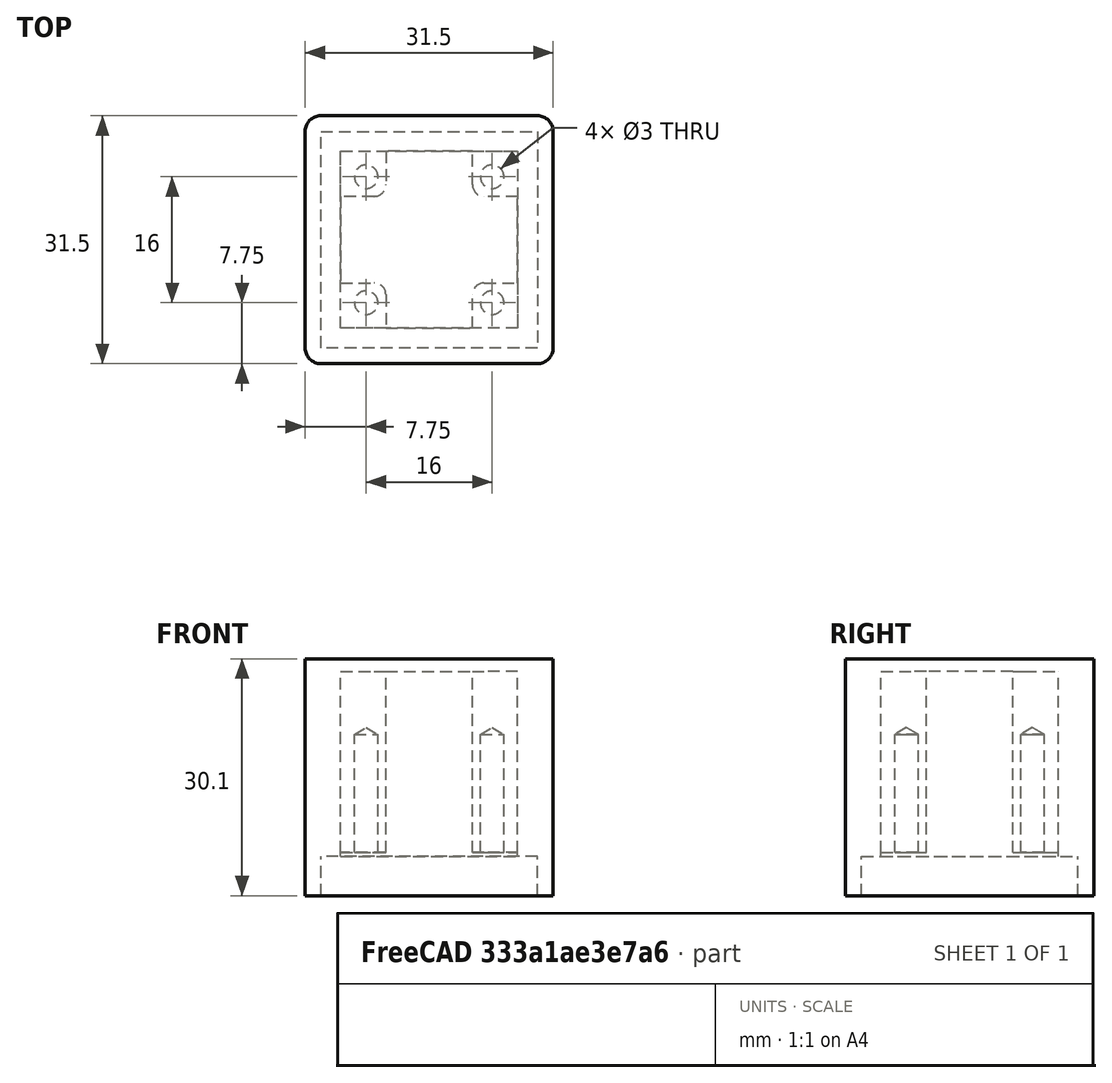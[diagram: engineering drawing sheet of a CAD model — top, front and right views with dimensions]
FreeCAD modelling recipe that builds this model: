
FCSTD DOCUMENT  (FreeCAD 1.1R44874 (Git))
Label: hood1slim_10x10x20
objects: Sketcher::SketchObject×6, PartDesign::Pocket×3, App::Point×1, PartDesign::Pad×1, PartDesign::Hole×1, Mesh::Feature×1, PartDesign::Body×1
note: 28 computed .brp shape members not serialized (recipe doc carries the construction recipe); baked Part::Feature solids carry a one-line shape summary decoded from their .brp

FEATURE [App::Point] Origin001
  Role = Origin
FEATURE [Sketcher::SketchObject] Sketch
  ArcFitTolerance = 1e-06
  AttachmentSupport = -> [Origin]
  ExternalTypes = [0]
  FullyConstrained = true
  MakeInternals = false
  MapMode = 5
  _ExternalGeoVersion = 1
  sketch-geometry (13):
    g0: LineSegment StartX=-13.75 StartY=-15.75 StartZ=0 EndX=13.75 EndY=-15.75 EndZ=0
    g1: LineSegment StartX=15.75 StartY=-13.75 StartZ=0 EndX=15.75 EndY=13.75 EndZ=0
    g2: LineSegment StartX=13.75 StartY=15.75 StartZ=0 EndX=-13.75 EndY=15.75 EndZ=0
    g3: LineSegment StartX=-15.75 StartY=13.75 StartZ=0 EndX=-15.75 EndY=-13.75 EndZ=0
    g4: GeomPoint [constr] X=0 Y=0 Z=0
    g5: ArcOfCircle CenterX=-13.75 CenterY=13.75 CenterZ=0 NormalX=0 NormalY=0 NormalZ=1 AngleXU=0 Radius=2 StartAngle=1.5708 EndAngle=3.14159
    g6: GeomPoint [constr] X=-15.75 Y=15.75 Z=0
    g7: ArcOfCircle CenterX=13.75 CenterY=13.75 CenterZ=0 NormalX=0 NormalY=0 NormalZ=1 AngleXU=0 Radius=2 StartAngle=0 EndAngle=1.5708
    g8: GeomPoint [constr] X=15.75 Y=15.75 Z=0
    g9: ArcOfCircle CenterX=13.75 CenterY=-13.75 CenterZ=0 NormalX=0 NormalY=0 NormalZ=1 AngleXU=0 Radius=2 StartAngle=4.71239 EndAngle=6.28319
    g10: GeomPoint [constr] X=15.75 Y=-15.75 Z=0
    g11: ArcOfCircle CenterX=-13.75 CenterY=-13.75 CenterZ=0 NormalX=0 NormalY=0 NormalZ=1 AngleXU=0 Radius=2 StartAngle=3.14159 EndAngle=4.71239
    g12: GeomPoint [constr] X=-15.75 Y=-15.75 Z=0
  constraints (28):
    c: Horizontal(g0)
    c: Horizontal(g2)
    c: Vertical(g1)
    c: Vertical(g3)
    c: Symmetric(g8,g12,g4)
    c: Distance(g10,g12) = 31.5
    c: Distance(g12,g6) = 31.5
    c: Coincident(g4,g-1)
    c: PointOnObject(g6,g3)
    c: PointOnObject(g6,g2)
    c: Tangent(g3,g5) = -1.5708
    c: Tangent(g2,g5) = -1.5708
    c: Radius(g5) = 2
    c: PointOnObject(g8,g1)
    c: PointOnObject(g8,g2)
    c: Tangent(g1,g7) = -1.5708
    c: Tangent(g2,g7) = -1.5708
    c: PointOnObject(g10,g1)
    c: PointOnObject(g10,g0)
    c: Tangent(g1,g9) = -1.5708
    c: Tangent(g0,g9) = -1.5708
    c: PointOnObject(g12,g0)
    c: PointOnObject(g12,g3)
    c: Tangent(g0,g11) = -1.5708
    c: Tangent(g3,g11) = -1.5708
    c: Equal(g5,g7)
    c: Equal(g5,g11)
    c: Equal(g5,g9)
FEATURE [PartDesign::Pad] Pad
  Direction = (0,0,1)
  Length = 30.1
  Length2 = 10
  Profile = -> Sketch
  ReferenceAxis = -> Sketch [N_Axis]
  Refine = true
  SideType = 0
  Suppressed = false
  Type = 0
  Type2 = 0
FEATURE [Sketcher::SketchObject] Sketch001
  ArcFitTolerance = 1e-06
  AttachmentSupport = -> [Pad]
  ExternalTypes = [0]
  FullyConstrained = true
  MakeInternals = false
  MapMode = 5
  Placement = pos=(0,0,0) rot=(1,0,0;3.14159rad)
  _ExternalGeoVersion = 1
  sketch-geometry (5):
    g0: LineSegment StartX=-13.75 StartY=-13.75 StartZ=0 EndX=13.75 EndY=-13.75 EndZ=0
    g1: LineSegment StartX=13.75 StartY=-13.75 StartZ=0 EndX=13.75 EndY=13.75 EndZ=0
    g2: LineSegment StartX=13.75 StartY=13.75 StartZ=0 EndX=-13.75 EndY=13.75 EndZ=0
    g3: LineSegment StartX=-13.75 StartY=13.75 StartZ=0 EndX=-13.75 EndY=-13.75 EndZ=0
    g4: GeomPoint [constr] X=0 Y=0 Z=0
  constraints (12):
    c: Coincident(g0,g1)
    c: Coincident(g1,g2)
    c: Coincident(g2,g3)
    c: Coincident(g3,g0)
    c: Horizontal(g0)
    c: Horizontal(g2)
    c: Vertical(g1)
    c: Vertical(g3)
    c: Symmetric(g2,g0,g4)
    c: Distance(g1,g3) = 27.5
    c: Distance(g0,g2) = 27.5
    c: Coincident(g4,g-1)
FEATURE [PartDesign::Pocket] Pocket
  BaseFeature = -> Pad
  Direction = (0,0,1)
  Length = 5
  Length2 = 5
  Profile = -> Sketch001
  ReferenceAxis = -> Sketch001 [N_Axis]
  Refine = true
  SideType = 0
  Suppressed = false
  Type = 0
  Type2 = 0
FEATURE [Sketcher::SketchObject] Sketch002
  ArcFitTolerance = 1e-06
  AttachmentSupport = -> [Pocket]
  ExternalTypes = [0]
  FullyConstrained = true
  MakeInternals = false
  MapMode = 5
  Placement = pos=(0,0,5) rot=(1,0,0;3.14159rad)
  _ExternalGeoVersion = 1
  sketch-geometry (5):
    g0: LineSegment StartX=-11.25 StartY=-11.25 StartZ=0 EndX=11.25 EndY=-11.25 EndZ=0
    g1: LineSegment StartX=11.25 StartY=-11.25 StartZ=0 EndX=11.25 EndY=11.25 EndZ=0
    g2: LineSegment StartX=11.25 StartY=11.25 StartZ=0 EndX=-11.25 EndY=11.25 EndZ=0
    g3: LineSegment StartX=-11.25 StartY=11.25 StartZ=0 EndX=-11.25 EndY=-11.25 EndZ=0
    g4: GeomPoint [constr] X=0 Y=0 Z=0
  constraints (12):
    c: Coincident(g0,g1)
    c: Coincident(g1,g2)
    c: Coincident(g2,g3)
    c: Coincident(g3,g0)
    c: Horizontal(g0)
    c: Horizontal(g2)
    c: Vertical(g1)
    c: Vertical(g3)
    c: Symmetric(g2,g0,g4)
    c: Distance(g1,g3) = 22.5
    c: Distance(g0,g2) = 22.5
    c: Coincident(g4,g-1)
FEATURE [PartDesign::Pocket] Pocket001
  BaseFeature = -> Pocket
  Direction = (0,0,1)
  Length = 0.5
  Length2 = 5
  Profile = -> Sketch002
  ReferenceAxis = -> Sketch002 [N_Axis]
  Refine = true
  SideType = 0
  Suppressed = false
  Type = 0
  Type2 = 0
FEATURE [Sketcher::SketchObject] Sketch003
  ArcFitTolerance = 1e-06
  AttachmentSupport = -> [Pocket001]
  ExternalTypes = [0]
  FullyConstrained = true
  MakeInternals = false
  MapMode = 5
  Placement = pos=(0,0,5.5) rot=(1,0,0;3.14159rad)
  _ExternalGeoVersion = 1
  sketch-geometry (4):
    g0: Circle CenterX=8 CenterY=8 CenterZ=0 NormalX=0 NormalY=0 NormalZ=1 AngleXU=0 Radius=1.5
    g1: Circle CenterX=-8 CenterY=8 CenterZ=0 NormalX=0 NormalY=0 NormalZ=1 AngleXU=0 Radius=1.5
    g2: Circle CenterX=-8 CenterY=-8 CenterZ=0 NormalX=0 NormalY=0 NormalZ=1 AngleXU=0 Radius=1.5
    g3: Circle CenterX=8 CenterY=-8 CenterZ=0 NormalX=0 NormalY=0 NormalZ=1 AngleXU=0 Radius=1.5
  constraints (9):
    c: Diameter(g0) = 3
    c: DistanceY(g-1,g0) = 8
    c: DistanceX(g-1,g0) = 8
    c: Equal(g0,g1)
    c: Equal(g0,g2)
    c: Equal(g0,g3)
    c: Symmetric(g1,g3,g-1)
    c: Symmetric(g0,g3,g-1)
    c: Symmetric(g2,g3,g-2)
FEATURE [PartDesign::Hole] Hole
  BaseFeature = -> Pocket001
  BaseProfileType = 7
  CustomThreadClearance = 0
  Depth = 15
  DepthType = 0
  Diameter = 3
  DrillForDepth = false
  DrillPoint = 1
  DrillPointAngle = 118
  HoleCutCountersinkAngle = 90
  HoleCutCustomValues = false
  HoleCutDepth = 0
  HoleCutDiameter = 0
  HoleCutType = 0
  ModelThread = false
  Profile = -> Sketch003
  Refine = true
  Suppressed = false
  Tapered = false
  TaperedAngle = 90
  ThreadClass = 0
  ThreadDepth = 15
  ThreadDepthType = 0
  ThreadDiameter = 3
  ThreadDirection = 0
  ThreadFit = 0
  ThreadSize = 0
  ThreadType = 0
  Threaded = false
  UseCustomThreadClearance = false
FEATURE [Sketcher::SketchObject] Sketch004
  ArcFitTolerance = 1e-06
  AttachmentSupport = -> [Hole]
  ExternalGeometry = -> [Sketch002]
  ExternalTypes = [0,0,0,0]
  FullyConstrained = true
  MakeInternals = false
  MapMode = 5
  Placement = pos=(0,0,5.5) rot=(1,0,0;3.14159rad)
  _ExternalGeoVersion = 1
  sketch-geometry (21):
    g0: GeomPoint [constr] X=0 Y=0 Z=0
    g1: LineSegment StartX=-11.25 StartY=-5.5 StartZ=0 EndX=-11.25 EndY=5.5 EndZ=0
    g2: LineSegment StartX=-11.25 StartY=5.5 StartZ=0 EndX=-7 EndY=5.5 EndZ=0
    g3: LineSegment StartX=-5.5 StartY=7 StartZ=0 EndX=-5.5 EndY=11.25 EndZ=0
    g4: LineSegment StartX=-5.5 StartY=11.25 StartZ=0 EndX=5.5 EndY=11.25 EndZ=0
    g5: LineSegment StartX=5.5 StartY=11.25 StartZ=0 EndX=5.5 EndY=7 EndZ=0
    g6: LineSegment StartX=7 StartY=5.5 StartZ=0 EndX=11.25 EndY=5.5 EndZ=0
    g7: LineSegment StartX=11.25 StartY=5.5 StartZ=0 EndX=11.25 EndY=-5.5 EndZ=0
    g8: LineSegment StartX=11.25 StartY=-5.5 StartZ=0 EndX=7 EndY=-5.5 EndZ=0
    g9: LineSegment StartX=5.5 StartY=-7 StartZ=0 EndX=5.5 EndY=-11.25 EndZ=0
    g10: LineSegment StartX=5.5 StartY=-11.25 StartZ=0 EndX=-5.5 EndY=-11.25 EndZ=0
    g11: LineSegment StartX=-5.5 StartY=-11.25 StartZ=0 EndX=-5.5 EndY=-7 EndZ=0
    g12: LineSegment StartX=-7 StartY=-5.5 StartZ=0 EndX=-11.25 EndY=-5.5 EndZ=0
    g13: ArcOfCircle CenterX=-7 CenterY=7 CenterZ=0 NormalX=0 NormalY=0 NormalZ=1 AngleXU=0 Radius=1.5 StartAngle=4.71239 EndAngle=6.28319
    g14: GeomPoint [constr] X=-5.5 Y=5.5 Z=0
    g15: ArcOfCircle CenterX=7 CenterY=7 CenterZ=0 NormalX=0 NormalY=0 NormalZ=1 AngleXU=0 Radius=1.5 StartAngle=3.14159 EndAngle=4.71239
    g16: GeomPoint [constr] X=5.5 Y=5.5 Z=0
    g17: ArcOfCircle CenterX=7 CenterY=-7 CenterZ=0 NormalX=0 NormalY=0 NormalZ=1 AngleXU=0 Radius=1.5 StartAngle=1.5708 EndAngle=3.14159
    g18: GeomPoint [constr] X=5.5 Y=-5.5 Z=0
    g19: ArcOfCircle CenterX=-7 CenterY=-7 CenterZ=0 NormalX=0 NormalY=0 NormalZ=1 AngleXU=0 Radius=1.5 StartAngle=0 EndAngle=1.5708
    g20: GeomPoint [constr] X=-5.5 Y=-5.5 Z=0
  constraints (46):
    c: Coincident(g0,g-1)
    c: Coincident(g1,g2)
    c: Horizontal(g2)
    c: Vertical(g3)
    c: Coincident(g3,g4)
    c: Coincident(g4,g5)
    c: Vertical(g5)
    c: Horizontal(g6)
    c: Coincident(g6,g7)
    c: Coincident(g7,g8)
    c: Vertical(g9)
    c: Coincident(g9,g10)
    c: Coincident(g10,g11)
    c: Coincident(g12,g1)
    c: Tangent(g4,g-3)
    c: Tangent(g1,g-4)
    c: Tangent(g7,g-6)
    c: Tangent(g10,g-5)
    c: DistanceY(g-1,g16) = 5.5
    c: DistanceX(g-1,g16) = 5.5
    c: Symmetric(g16,g18,g-1)
    c: Symmetric(g16,g14,g-2)
    c: Symmetric(g18,g20,g-2)
    c: Parallel(g6,g8)
    c: Parallel(g2,g12)
    c: Parallel(g9,g11)
    c: PointOnObject(g14,g3)
    c: PointOnObject(g14,g2)
    c: Tangent(g3,g13) = -1.5708
    c: Tangent(g2,g13) = -1.5708
    c: Radius(g13) = 1.5
    c: PointOnObject(g16,g5)
    c: PointOnObject(g16,g6)
    c: Tangent(g5,g15) = -1.5708
    c: Tangent(g6,g15) = -1.5708
    c: PointOnObject(g18,g8)
    c: PointOnObject(g18,g9)
    c: Tangent(g8,g17) = -1.5708
    c: Tangent(g9,g17) = -1.5708
    c: PointOnObject(g20,g12)
    c: PointOnObject(g20,g11)
    c: Tangent(g12,g19) = -1.5708
    c: Tangent(g11,g19) = -1.5708
    c: Equal(g13,g15)
    c: Equal(g13,g19)
    c: Equal(g13,g17)
FEATURE [PartDesign::Pocket] Pocket002
  BaseFeature = -> Hole
  Direction = (0,0,1)
  Length = 23
  Length2 = 5
  Profile = -> Sketch004
  ReferenceAxis = -> Sketch004 [N_Axis]
  Refine = true
  SideType = 0
  Suppressed = false
  Type = 0
  Type2 = 0
FEATURE [Mesh::Feature] Mesh  label="Body (Meshed)"
FEATURE [Sketcher::SketchObject] Sketch005
  ArcFitTolerance = 1e-06
  AttachmentSupport = -> [Pocket002]
  ExternalTypes = [0]
  FullyConstrained = true
  MakeInternals = false
  MapMode = 5
  Placement = pos=(0,0,28.5) rot=(1,0,0;3.14159rad)
  _ExternalGeoVersion = 1
FEATURE [PartDesign::Body] Body
  AllowCompound = true
  Group = -> [Sketch,Pad,Sketch001,Pocket,Sketch002,Pocket001,Sketch003,Hole,Sketch004,Pocket002,Sketch005]
  Origin = -> Origin
  Tip = -> Pocket002
